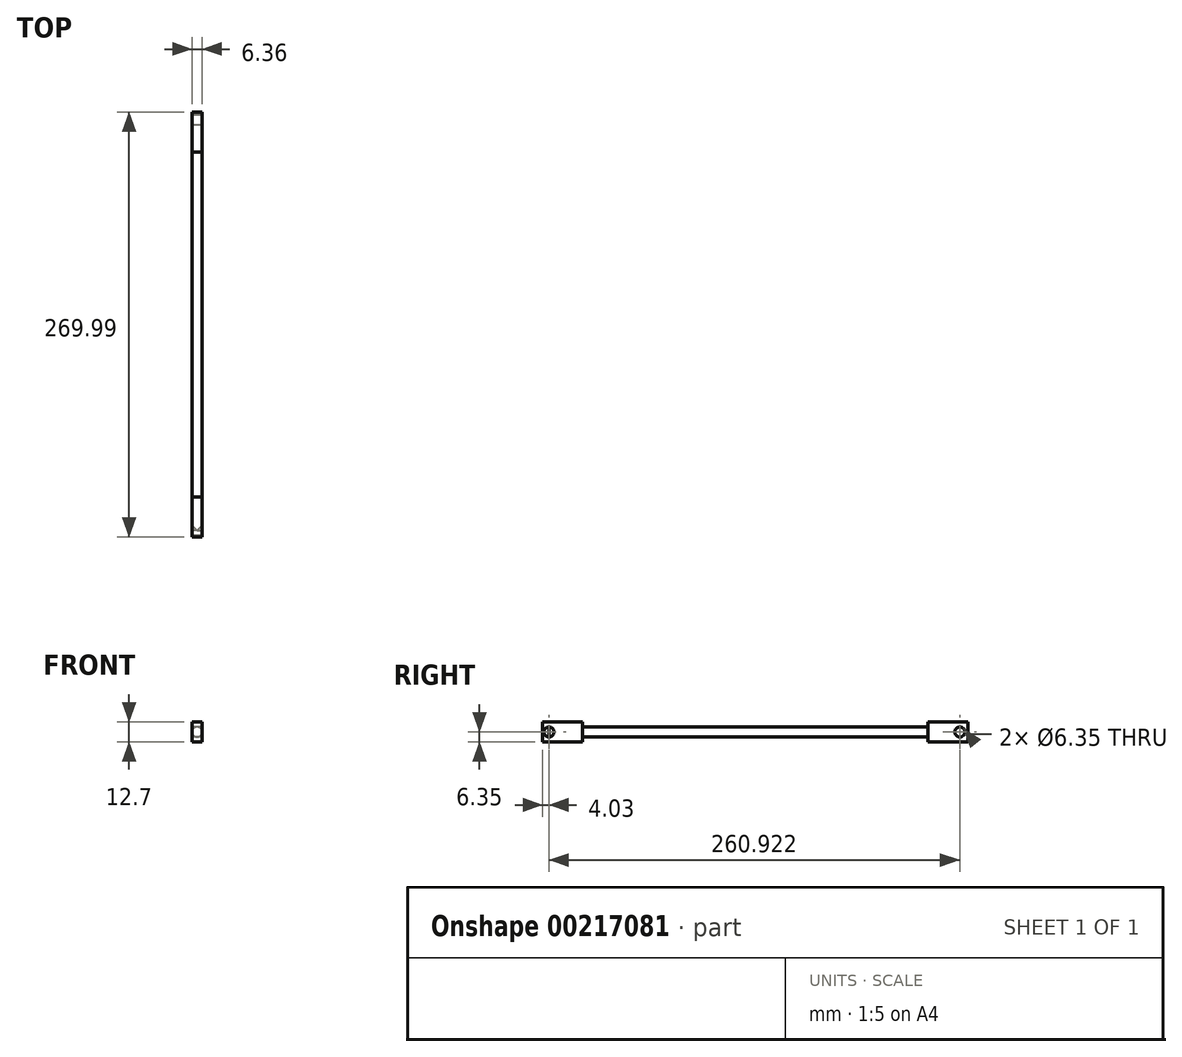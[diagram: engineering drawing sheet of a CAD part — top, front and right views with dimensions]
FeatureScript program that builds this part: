
annotation { "Feature Type Name" : "Feature", "Feature Type Description" : "" }
export const myFeature = defineFeature(function(context is Context, id is Id, definition is map)
    precondition{}
    {
        {
            var Q0;
            Q0=qCreatedBy(makeId("Right.planeOp"),FACE);
            var sketch = newSketch(context, id + "F0", { "sketchPlane" : qUnion([Q0])});
            skCircle(sketch, "E0", {"center": v(0, 0) * mm, "radius": 3.18 * mm});
            skLineSegment(sketch, "E1.bottom", {"start": v(21.37, -6.35) * mm, "end": v(-4.03, -6.35) * mm});
            skLineSegment(sketch, "E1.top", {"start": v(21.37, 6.35) * mm, "end": v(-4.03, 6.35) * mm});
            skLineSegment(sketch, "E1.left", {"start": v(21.37, -6.35) * mm, "end": v(21.37, 6.35) * mm});
            skLineSegment(sketch, "E1.right", {"start": v(-4.03, -6.35) * mm, "end": v(-4.03, 6.35) * mm});
            skPoint(sketch, "E1.middle", {"position": v(8.67, 0) * mm});
            skSolve(sketch);
        }
        {
            var Q0;
            Q0=qCreatedBy(makeId("Front.planeOp"),FACE);
            var sketch = newSketch(context, id + "F1", { "sketchPlane" : qUnion([Q0])});
            skCircle(sketch, "E2", {"center": v(0, 0) * mm, "radius": 3.18 * mm});
            skSolve(sketch);
        }
        {
            var Q0;
            Q0=makeQuery(id+"F1.imprint","IMPRINT",FACE,{"disambiguationData":[TD([[makeQuery(id+"F1.imprint","IMPRINT",EDGE,{"derivedFrom":sQuery(id+"F1.wireOp",EDGE,"E2")}),1.0]])]});
            extrude(context, id + "F2", {"entities" : qUnion([Q0]), "oppositeDirection" : true, "depth" : 254 * mm});
        }
        {
            var Q0;
            Q0=makeQuery(id+"F0.imprint","IMPRINT",FACE,{"disambiguationData":[TD([[makeQuery(id+"F0.imprint","IMPRINT",EDGE,{"derivedFrom":sQuery(id+"F0.wireOp",EDGE,"E0")}),-1.0]])]});
            extrude(context, id + "F3", {"entities" : qUnion([Q0]), "operationType" : NewBodyOperationType.ADD, "depth" : 6.35 * mm, "symmetric" : true});
        }
        {
            var Q0;
            Q0=qCreatedBy(makeId("Right.planeOp"),FACE);
            var sketch = newSketch(context, id + "F4", { "sketchPlane" : qUnion([Q0])});
            skLineSegment(sketch, "E3.bottom", {"start": v(265.96, -6.35) * mm, "end": v(240.56, -6.35) * mm});
            skLineSegment(sketch, "E3.top", {"start": v(265.96, 6.35) * mm, "end": v(240.56, 6.35) * mm});
            skLineSegment(sketch, "E3.left", {"start": v(265.96, -6.35) * mm, "end": v(265.96, 6.35) * mm});
            skLineSegment(sketch, "E3.right", {"start": v(240.56, -6.35) * mm, "end": v(240.56, 6.35) * mm});
            skPoint(sketch, "E3.middle", {"position": v(253.26, 0) * mm});
            skCircle(sketch, "E4", {"center": v(260.92, 0) * mm, "radius": 3.18 * mm});
            skSolve(sketch);
        }
        {
            var Q0;
            Q0=makeQuery(id+"F4.imprint","IMPRINT",FACE,{"disambiguationData":[TD([[makeQuery(id+"F4.imprint","IMPRINT",EDGE,{"derivedFrom":sQuery(id+"F4.wireOp",EDGE,"E3.bottom")}),-1.0]])]});
            extrude(context, id + "F5", {"entities" : qUnion([Q0]), "operationType" : NewBodyOperationType.ADD, "depth" : 6.35 * mm, "symmetric" : true});
        }
    });
